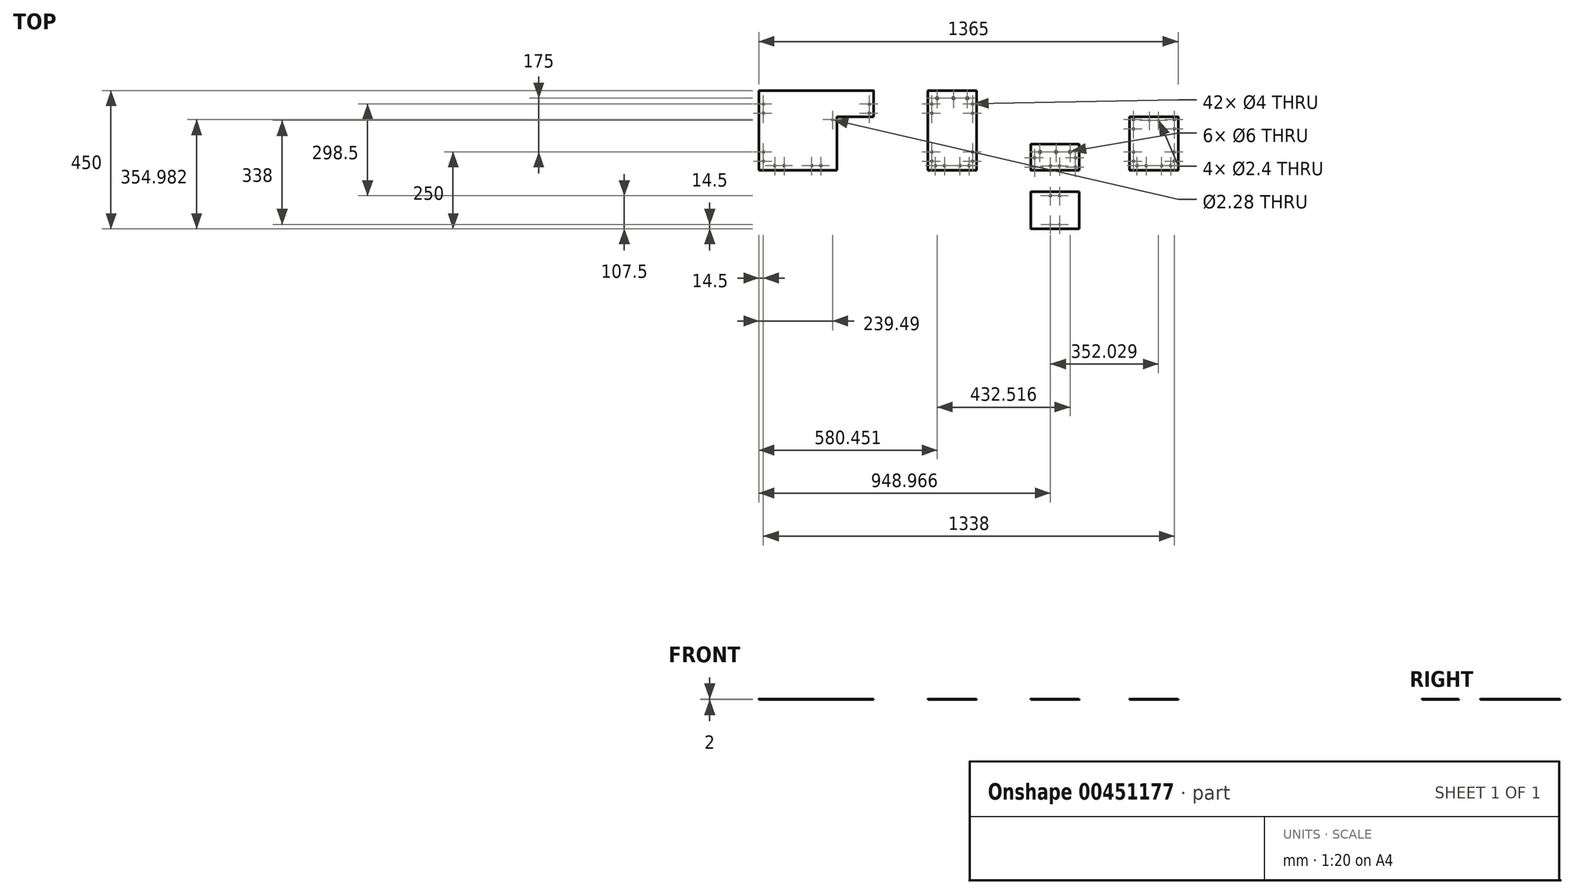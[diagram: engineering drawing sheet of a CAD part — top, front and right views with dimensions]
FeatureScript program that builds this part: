
annotation { "Feature Type Name" : "Feature", "Feature Type Description" : "" }
export const myFeature = defineFeature(function(context is Context, id is Id, definition is map)
    precondition{}
    {
        {
            var Q0;
            Q0=qCreatedBy(makeId("Top.planeOp"),FACE);
            var sketch = newSketch(context, id + "F0", { "sketchPlane" : qUnion([Q0])});
            skLineSegment(sketch, "E0.bottom", {"start": v(374, 0) * mm, "end": v(0, 0) * mm});
            skLineSegment(sketch, "E0.top", {"start": v(374, 260) * mm, "end": v(0, 260) * mm});
            skLineSegment(sketch, "E0.left", {"start": v(374, 0) * mm, "end": v(374, 260) * mm});
            skLineSegment(sketch, "E0.right", {"start": v(0, 0) * mm, "end": v(0, 260) * mm});
            skPoint(sketch, "E0.middle", {"position": v(187, 130) * mm});
            skLineSegment(sketch, "E1.bottom", {"start": v(708.45, 0) * mm, "end": v(550.45, 0) * mm});
            skLineSegment(sketch, "E1.top", {"start": v(708.45, 260) * mm, "end": v(550.45, 260) * mm});
            skLineSegment(sketch, "E1.left", {"start": v(708.45, 0) * mm, "end": v(708.45, 260) * mm});
            skLineSegment(sketch, "E1.right", {"start": v(550.45, 0) * mm, "end": v(550.45, 260) * mm});
            skPoint(sketch, "E1.middle", {"position": v(629.45, 130) * mm});
            skLineSegment(sketch, "E2.bottom", {"start": v(1042.97, 0) * mm, "end": v(884.97, 0) * mm});
            skLineSegment(sketch, "E2.top", {"start": v(1042.97, 85) * mm, "end": v(884.97, 85) * mm});
            skLineSegment(sketch, "E2.left", {"start": v(1042.97, 0) * mm, "end": v(1042.97, 85) * mm});
            skLineSegment(sketch, "E2.right", {"start": v(884.97, 0) * mm, "end": v(884.97, 85) * mm});
            skPoint(sketch, "E2.middle", {"position": v(963.97, 42.5) * mm});
            skLineSegment(sketch, "E3.bottom", {"start": v(1365, 175) * mm, "end": v(1207, 175) * mm});
            skLineSegment(sketch, "E3.top", {"start": v(1365, 0) * mm, "end": v(1207, 0) * mm});
            skLineSegment(sketch, "E3.left", {"start": v(1207, 0) * mm, "end": v(1207, 175) * mm});
            skLineSegment(sketch, "E3.right", {"start": v(1365, 0) * mm, "end": v(1365, 175) * mm});
            skPoint(sketch, "E3.middle", {"position": v(1286, 87.5) * mm});
            skCircle(sketch, "E4", {"center": v(62, 206) * mm, "radius": 1.5 * mm, "construction": true});
            skCircle(sketch, "E5", {"center": v(102, 206) * mm, "radius": 1.5 * mm, "construction": true});
            skLineSegment(sketch, "E6", {"start": v(187, 130) * mm, "end": v(187, 165.07) * mm, "construction": true});
            skLineSegment(sketch, "E7.bottom", {"start": v(917.97, 57) * mm, "end": v(911.97, 57) * mm, "construction": true});
            skLineSegment(sketch, "E7.top", {"start": v(917.97, 63) * mm, "end": v(911.97, 63) * mm, "construction": true});
            skLineSegment(sketch, "E7.left", {"start": v(917.97, 57) * mm, "end": v(917.97, 63) * mm, "construction": true});
            skLineSegment(sketch, "E7.right", {"start": v(911.97, 57) * mm, "end": v(911.97, 63) * mm, "construction": true});
            skPoint(sketch, "E7.middle", {"position": v(914.97, 60) * mm});
            skArc(sketch, "E8", {"start": v(917.97, 63) * mm, "mid": v(914.97, 66) * mm, "end": v(911.97, 63) * mm, "construction": true});
            skArc(sketch, "E9", {"start": v(911.97, 57) * mm, "mid": v(914.97, 54) * mm, "end": v(917.97, 57) * mm, "construction": true});
            skLineSegment(sketch, "E10.bottom", {"start": v(970.97, 57) * mm, "end": v(964.97, 57) * mm, "construction": true});
            skLineSegment(sketch, "E10.top", {"start": v(970.97, 63) * mm, "end": v(964.97, 63) * mm, "construction": true});
            skLineSegment(sketch, "E10.left", {"start": v(970.97, 57) * mm, "end": v(970.97, 63) * mm, "construction": true});
            skLineSegment(sketch, "E10.right", {"start": v(964.97, 57) * mm, "end": v(964.97, 63) * mm, "construction": true});
            skPoint(sketch, "E10.middle", {"position": v(967.97, 60) * mm});
            skArc(sketch, "E11", {"start": v(970.97, 63) * mm, "mid": v(967.97, 66) * mm, "end": v(964.97, 63) * mm, "construction": true});
            skArc(sketch, "E12", {"start": v(964.97, 57) * mm, "mid": v(967.97, 54) * mm, "end": v(970.97, 57) * mm, "construction": true});
            skLineSegment(sketch, "E13.bottom", {"start": v(1015.97, 57) * mm, "end": v(1009.97, 57) * mm, "construction": true});
            skLineSegment(sketch, "E13.top", {"start": v(1015.97, 63) * mm, "end": v(1009.97, 63) * mm, "construction": true});
            skLineSegment(sketch, "E13.left", {"start": v(1015.97, 57) * mm, "end": v(1015.97, 63) * mm, "construction": true});
            skLineSegment(sketch, "E13.right", {"start": v(1009.97, 57) * mm, "end": v(1009.97, 63) * mm, "construction": true});
            skPoint(sketch, "E13.middle", {"position": v(1012.97, 60) * mm});
            skArc(sketch, "E14", {"start": v(1015.97, 63) * mm, "mid": v(1012.97, 66) * mm, "end": v(1009.97, 63) * mm, "construction": true});
            skArc(sketch, "E15", {"start": v(1009.97, 57) * mm, "mid": v(1012.97, 54) * mm, "end": v(1015.97, 57) * mm, "construction": true});
            skLineSegment(sketch, "E16.bottom", {"start": v(64, 202) * mm, "end": v(60, 202) * mm, "construction": true});
            skLineSegment(sketch, "E16.top", {"start": v(64, 210) * mm, "end": v(60, 210) * mm, "construction": true});
            skLineSegment(sketch, "E16.left", {"start": v(64, 202) * mm, "end": v(64, 210) * mm, "construction": true});
            skLineSegment(sketch, "E16.right", {"start": v(60, 202) * mm, "end": v(60, 210) * mm, "construction": true});
            skArc(sketch, "E17", {"start": v(64, 210) * mm, "mid": v(62, 212) * mm, "end": v(60, 210) * mm, "construction": true});
            skArc(sketch, "E18", {"start": v(60, 202) * mm, "mid": v(62, 200) * mm, "end": v(64, 202) * mm, "construction": true});
            skLineSegment(sketch, "E19.bottom", {"start": v(104, 202) * mm, "end": v(100, 202) * mm, "construction": true});
            skLineSegment(sketch, "E19.top", {"start": v(104, 210) * mm, "end": v(100, 210) * mm, "construction": true});
            skLineSegment(sketch, "E19.left", {"start": v(104, 202) * mm, "end": v(104, 210) * mm, "construction": true});
            skLineSegment(sketch, "E19.right", {"start": v(100, 202) * mm, "end": v(100, 210) * mm, "construction": true});
            skArc(sketch, "E20", {"start": v(104, 210) * mm, "mid": v(102, 212) * mm, "end": v(100, 210) * mm, "construction": true});
            skArc(sketch, "E21", {"start": v(100, 202) * mm, "mid": v(102, 200) * mm, "end": v(104, 202) * mm, "construction": true});
            skLineSegment(sketch, "E22.MirrorCS", {"start": v(270, 210) * mm, "end": v(274, 210) * mm, "construction": true});
            skLineSegment(sketch, "E23.MirrorCS", {"start": v(270, 202) * mm, "end": v(274, 202) * mm, "construction": true});
            skArc(sketch, "E24.MirrorCS", {"start": v(274, 202) * mm, "mid": v(272, 200) * mm, "end": v(270, 202) * mm, "construction": true});
            skLineSegment(sketch, "E25.MirrorCS", {"start": v(274, 202) * mm, "end": v(274, 210) * mm, "construction": true});
            skLineSegment(sketch, "E26.MirrorCS", {"start": v(270, 202) * mm, "end": v(270, 210) * mm, "construction": true});
            skArc(sketch, "E27.MirrorCS", {"start": v(270, 210) * mm, "mid": v(272, 212) * mm, "end": v(274, 210) * mm, "construction": true});
            skPoint(sketch, "E28.MirrorP", {"position": v(272, 206) * mm});
            skArc(sketch, "E29.MirrorCS", {"start": v(314, 202) * mm, "mid": v(312, 200) * mm, "end": v(310, 202) * mm, "construction": true});
            skLineSegment(sketch, "E30.MirrorCS", {"start": v(310, 202) * mm, "end": v(314, 202) * mm, "construction": true});
            skLineSegment(sketch, "E31.MirrorCS", {"start": v(310, 210) * mm, "end": v(314, 210) * mm, "construction": true});
            skLineSegment(sketch, "E32.MirrorCS", {"start": v(314, 202) * mm, "end": v(314, 210) * mm, "construction": true});
            skLineSegment(sketch, "E33.MirrorCS", {"start": v(310, 202) * mm, "end": v(310, 210) * mm, "construction": true});
            skArc(sketch, "E34.MirrorCS", {"start": v(310, 210) * mm, "mid": v(312, 212) * mm, "end": v(314, 210) * mm, "construction": true});
            skPoint(sketch, "E35.MirrorP", {"position": v(312, 206) * mm});
            skCircle(sketch, "E36", {"center": v(580.45, 235) * mm, "radius": 3 * mm});
            skCircle(sketch, "E37", {"center": v(633.45, 235) * mm, "radius": 3 * mm});
            skCircle(sketch, "E38", {"center": v(678.45, 235) * mm, "radius": 3 * mm});
            skLineSegment(sketch, "E39.bottom", {"start": v(1042.97, -70) * mm, "end": v(884.97, -70) * mm});
            skLineSegment(sketch, "E39.top", {"start": v(1042.97, -190) * mm, "end": v(884.97, -190) * mm});
            skLineSegment(sketch, "E39.left", {"start": v(1042.97, -70) * mm, "end": v(1042.97, -190) * mm});
            skLineSegment(sketch, "E39.right", {"start": v(884.97, -70) * mm, "end": v(884.97, -190) * mm});
            skPoint(sketch, "E39.middle", {"position": v(963.97, -130) * mm});
            skCircle(sketch, "E40", {"center": v(914.97, 60) * mm, "radius": 3 * mm});
            skCircle(sketch, "E41", {"center": v(967.97, 60) * mm, "radius": 3 * mm});
            skCircle(sketch, "E42", {"center": v(1012.97, 60) * mm, "radius": 3 * mm});
            skCircle(sketch, "E43", {"center": v(574.45, 15.5) * mm, "radius": 2 * mm});
            skCircle(sketch, "E44", {"center": v(604.45, 15.5) * mm, "radius": 2 * mm});
            skLineSegment(sketch, "E45", {"start": v(629.45, 142.28) * mm, "end": v(629.45, 157.74) * mm, "construction": true});
            skCircle(sketch, "E46.MirrorC", {"center": v(684.45, 15.5) * mm, "radius": 2 * mm});
            skCircle(sketch, "E47.MirrorC", {"center": v(654.45, 15.5) * mm, "radius": 2 * mm});
            skCircle(sketch, "E48", {"center": v(1231, 15.5) * mm, "radius": 2 * mm});
            skCircle(sketch, "E49", {"center": v(1261, 15.5) * mm, "radius": 2 * mm});
            skLineSegment(sketch, "E50", {"start": v(1286, 97.83) * mm, "end": v(1286, 112.31) * mm, "construction": true});
            skCircle(sketch, "E51.MirrorC", {"center": v(1311, 15.5) * mm, "radius": 2 * mm});
            skCircle(sketch, "E52.MirrorC", {"center": v(1341, 15.5) * mm, "radius": 2 * mm});
            skCircle(sketch, "E53", {"center": v(695.95, 216) * mm, "radius": 2 * mm});
            skCircle(sketch, "E54", {"center": v(695.95, 186) * mm, "radius": 2 * mm});
            skLineSegment(sketch, "E55", {"start": v(689.83, 221) * mm, "end": v(700.87, 221) * mm, "construction": true});
            skCircle(sketch, "E56.MirrorC", {"center": v(562.95, 216) * mm, "radius": 2 * mm});
            skCircle(sketch, "E57.MirrorC", {"center": v(562.95, 186) * mm, "radius": 2 * mm});
            skLineSegment(sketch, "E58", {"start": v(648.13, 130) * mm, "end": v(662.37, 130) * mm, "construction": true});
            skCircle(sketch, "E59.MirrorC", {"center": v(695.95, 60) * mm, "radius": 2 * mm});
            skCircle(sketch, "E60.MirrorC", {"center": v(695.95, 30) * mm, "radius": 2 * mm});
            skCircle(sketch, "E61", {"center": v(1030.47, 41) * mm, "radius": 2 * mm});
            skCircle(sketch, "E62", {"center": v(1030.47, 11) * mm, "radius": 2 * mm});
            skLineSegment(sketch, "E63", {"start": v(963.97, 51.85) * mm, "end": v(963.97, 57.94) * mm, "construction": true});
            skCircle(sketch, "E64.MirrorC", {"center": v(897.47, 11) * mm, "radius": 2 * mm});
            skCircle(sketch, "E65.MirrorC", {"center": v(897.47, 41) * mm, "radius": 2 * mm});
            skCircle(sketch, "E66", {"center": v(1352.5, 60) * mm, "radius": 2 * mm});
            skCircle(sketch, "E67", {"center": v(1352.5, 30) * mm, "radius": 2 * mm});
            skCircle(sketch, "E68.MirrorC", {"center": v(1219.5, 30) * mm, "radius": 2 * mm});
            skCircle(sketch, "E69.MirrorC", {"center": v(1219.5, 60) * mm, "radius": 2 * mm});
            skCircle(sketch, "E70.MirrorC", {"center": v(562.95, 60) * mm, "radius": 2 * mm});
            skCircle(sketch, "E71.MirrorC", {"center": v(562.95, 30) * mm, "radius": 2 * mm});
            skCircle(sketch, "E72", {"center": v(1352.5, 165) * mm, "radius": 2 * mm});
            skCircle(sketch, "E73", {"center": v(1352.5, 135) * mm, "radius": 2 * mm});
            skCircle(sketch, "E74.MirrorC", {"center": v(1219.5, 135) * mm, "radius": 2 * mm});
            skCircle(sketch, "E75.MirrorC", {"center": v(1219.5, 165) * mm, "radius": 2 * mm});
            skCircle(sketch, "E76", {"center": v(14.5, 60) * mm, "radius": 2 * mm});
            skCircle(sketch, "E77", {"center": v(14.5, 30) * mm, "radius": 2 * mm});
            skCircle(sketch, "E78", {"center": v(14.5, 216) * mm, "radius": 2 * mm});
            skCircle(sketch, "E79", {"center": v(14.5, 186) * mm, "radius": 2 * mm});
            skCircle(sketch, "E80.MirrorC", {"center": v(359.5, 186) * mm, "radius": 2 * mm});
            skCircle(sketch, "E81.MirrorC", {"center": v(359.5, 216) * mm, "radius": 2 * mm});
            skCircle(sketch, "E82", {"center": v(978.97, 14.5) * mm, "radius": 2 * mm});
            skCircle(sketch, "E83", {"center": v(948.97, 14.5) * mm, "radius": 2 * mm});
            skCircle(sketch, "E84", {"center": v(948.97, -82.5) * mm, "radius": 2 * mm});
            skCircle(sketch, "E85", {"center": v(978.97, -82.5) * mm, "radius": 2 * mm});
            skCircle(sketch, "E86", {"center": v(948.97, -175.5) * mm, "radius": 1.2 * mm});
            skCircle(sketch, "E87", {"center": v(978.97, -175.5) * mm, "radius": 1.2 * mm});
            skCircle(sketch, "E88", {"center": v(1301, 162.5) * mm, "radius": 1.2 * mm});
            skCircle(sketch, "E89", {"center": v(1271, 162.5) * mm, "radius": 1.2 * mm});
            skCircle(sketch, "E90", {"center": v(239.5, 164.98) * mm, "radius": 1.14 * mm});
            skSolve(sketch);
        }
        {
            var Q0;
            Q0 = qSketchRegion(id + "F0", true);
            extrude(context, id + "F1", {"entities" : qUnion([Q0]), "depth" : 2 * mm, "offsetDistance" : 25 * mm});
        }
        {
            var Q0;
            Q0=makeQuery(id+"F1.opExtrude","CAP_FACE",FACE,{"disambiguationData":[OSD([sQuery(id+"F0.wireOp",EDGE,"E0.bottom"),sQuery(id+"F0.wireOp",EDGE,"E0.top"),sQuery(id+"F0.wireOp",EDGE,"E0.left"),sQuery(id+"F0.wireOp",EDGE,"E0.right"),sQuery(id+"F0.wireOp",EDGE,"E4"),sQuery(id+"F0.wireOp",EDGE,"E5"),sQuery(id+"F0.wireOp",EDGE,"4ba7c3d7-5d5b-46dc-9287-b6db8c2c33c00.MirrorC"),sQuery(id+"F0.wireOp",EDGE,"4ba7c3d7-5d5b-46dc-9287-b6db8c2c33c01.MirrorC")])],"isStart":false});
            var sketch = newSketch(context, id + "F2", { "sketchPlane" : qUnion([Q0])});
            skLineSegment(sketch, "E91.bottom", {"start": v(374, 0) * mm, "end": v(254, 0) * mm});
            skLineSegment(sketch, "E91.top", {"start": v(374, 175) * mm, "end": v(254, 175) * mm});
            skLineSegment(sketch, "E91.left", {"start": v(374, 0) * mm, "end": v(374, 175) * mm});
            skLineSegment(sketch, "E91.right", {"start": v(254, 0) * mm, "end": v(254, 175) * mm});
            skLineSegment(sketch, "E92", {"start": v(127, 64.28) * mm, "end": v(127, 23.94) * mm, "construction": true});
            skCircle(sketch, "E93", {"center": v(52, 15.5) * mm, "radius": 2 * mm});
            skCircle(sketch, "E94", {"center": v(82, 15.5) * mm, "radius": 2 * mm});
            skCircle(sketch, "E95.MirrorC", {"center": v(172, 15.5) * mm, "radius": 2 * mm});
            skCircle(sketch, "E96.MirrorC", {"center": v(202, 15.5) * mm, "radius": 2 * mm});
            skSolve(sketch);
        }
        {
            var Q0;
            Q0 = qSketchRegion(id + "F2", true);
            extrude(context, id + "F3", {"entities" : qUnion([Q0]), "operationType" : NewBodyOperationType.REMOVE, "oppositeDirection" : true, "depth" : 25 * mm, "offsetDistance" : 25 * mm});
        }
        {
            var Q0;
            Q0=makeQuery(id+"F1.opExtrude","SWEPT_EDGE",EDGE,{"disambiguationData":[OSD([sQuery(id+"F0.wireOp",EDGE,"E2.top"),sQuery(id+"F0.wireOp",EDGE,"E2.left")])]});
            var Q1;
            Q1=makeQuery(id+"F1.opExtrude","SWEPT_EDGE",EDGE,{"disambiguationData":[OSD([sQuery(id+"F0.wireOp",EDGE,"E2.bottom"),sQuery(id+"F0.wireOp",EDGE,"E2.left")])]});
            var Q2;
            Q2=makeQuery(id+"F1.opExtrude","SWEPT_EDGE",EDGE,{"disambiguationData":[OSD([sQuery(id+"F0.wireOp",EDGE,"E2.bottom"),sQuery(id+"F0.wireOp",EDGE,"E2.right")])]});
            var Q3;
            Q3=makeQuery(id+"F1.opExtrude","SWEPT_EDGE",EDGE,{"disambiguationData":[OSD([sQuery(id+"F0.wireOp",EDGE,"E2.top"),sQuery(id+"F0.wireOp",EDGE,"E2.right")])]});
            var Q4;
            Q4=makeQuery(id+"F1.opExtrude","SWEPT_EDGE",EDGE,{"disambiguationData":[OSD([sQuery(id+"F0.wireOp",EDGE,"E0.top"),sQuery(id+"F0.wireOp",EDGE,"E0.right")])]});
            var Q5;
            Q5=makeQuery(id+"F1.opExtrude","SWEPT_EDGE",EDGE,{"disambiguationData":[OSD([sQuery(id+"F0.wireOp",EDGE,"E0.bottom"),sQuery(id+"F0.wireOp",EDGE,"E0.right")])]});
            var Q6;
            Q6=makeQuery(id+"F3.boolean.opBoolean","COPY",EDGE,{"derivedFrom":makeQuery(id+"F3.opExtrude","SWEPT_EDGE",EDGE,{"disambiguationData":[OSD([sQuery(id+"F0.wireOp",EDGE,"E0.bottom"),sQuery(id+"F2.wireOp",EDGE,"E91.bottom"),sQuery(id+"F2.wireOp",EDGE,"E91.right")])]})});
            var Q7;
            Q7=makeQuery(id+"F3.boolean.opBoolean","COPY",EDGE,{"derivedFrom":makeQuery(id+"F3.opExtrude","SWEPT_EDGE",EDGE,{"disambiguationData":[OSD([sQuery(id+"F2.wireOp",EDGE,"E91.top"),sQuery(id+"F2.wireOp",EDGE,"E91.right")])]})});
            var Q8;
            Q8=makeQuery(id+"F3.boolean.opBoolean","COPY",EDGE,{"derivedFrom":makeQuery(id+"F3.opExtrude","SWEPT_EDGE",EDGE,{"disambiguationData":[OSD([sQuery(id+"F0.wireOp",EDGE,"E0.left"),sQuery(id+"F2.wireOp",EDGE,"E91.top"),sQuery(id+"F2.wireOp",EDGE,"E91.left")])]})});
            var Q9;
            Q9=makeQuery(id+"F1.opExtrude","SWEPT_EDGE",EDGE,{"disambiguationData":[OSD([sQuery(id+"F0.wireOp",EDGE,"E0.top"),sQuery(id+"F0.wireOp",EDGE,"E0.left")])]});
            var Q10;
            Q10=makeQuery(id+"F1.opExtrude","SWEPT_EDGE",EDGE,{"disambiguationData":[OSD([sQuery(id+"F0.wireOp",EDGE,"E1.top"),sQuery(id+"F0.wireOp",EDGE,"E1.right")])]});
            var Q11;
            Q11=makeQuery(id+"F1.opExtrude","SWEPT_EDGE",EDGE,{"disambiguationData":[OSD([sQuery(id+"F0.wireOp",EDGE,"E1.top"),sQuery(id+"F0.wireOp",EDGE,"E1.left")])]});
            var Q12;
            Q12=makeQuery(id+"F1.opExtrude","SWEPT_EDGE",EDGE,{"disambiguationData":[OSD([sQuery(id+"F0.wireOp",EDGE,"E1.bottom"),sQuery(id+"F0.wireOp",EDGE,"E1.left")])]});
            var Q13;
            Q13=makeQuery(id+"F1.opExtrude","SWEPT_EDGE",EDGE,{"disambiguationData":[OSD([sQuery(id+"F0.wireOp",EDGE,"E1.bottom"),sQuery(id+"F0.wireOp",EDGE,"E1.right")])]});
            var Q14;
            Q14=makeQuery(id+"F1.opExtrude","SWEPT_EDGE",EDGE,{"disambiguationData":[OSD([sQuery(id+"F0.wireOp",EDGE,"E39.bottom"),sQuery(id+"F0.wireOp",EDGE,"E39.right")])]});
            var Q15;
            Q15=makeQuery(id+"F1.opExtrude","SWEPT_EDGE",EDGE,{"disambiguationData":[OSD([sQuery(id+"F0.wireOp",EDGE,"E39.top"),sQuery(id+"F0.wireOp",EDGE,"E39.right")])]});
            var Q16;
            Q16=makeQuery(id+"F1.opExtrude","SWEPT_EDGE",EDGE,{"disambiguationData":[OSD([sQuery(id+"F0.wireOp",EDGE,"E39.bottom"),sQuery(id+"F0.wireOp",EDGE,"E39.left")])]});
            var Q17;
            Q17=makeQuery(id+"F1.opExtrude","SWEPT_EDGE",EDGE,{"disambiguationData":[OSD([sQuery(id+"F0.wireOp",EDGE,"E39.top"),sQuery(id+"F0.wireOp",EDGE,"E39.left")])]});
            var Q18;
            Q18=makeQuery(id+"F1.opExtrude","SWEPT_EDGE",EDGE,{"disambiguationData":[OSD([sQuery(id+"F0.wireOp",EDGE,"E3.bottom"),sQuery(id+"F0.wireOp",EDGE,"E3.left")])]});
            var Q19;
            Q19=makeQuery(id+"F1.opExtrude","SWEPT_EDGE",EDGE,{"disambiguationData":[OSD([sQuery(id+"F0.wireOp",EDGE,"E3.top"),sQuery(id+"F0.wireOp",EDGE,"E3.left")])]});
            var Q20;
            Q20=makeQuery(id+"F1.opExtrude","SWEPT_EDGE",EDGE,{"disambiguationData":[OSD([sQuery(id+"F0.wireOp",EDGE,"E3.bottom"),sQuery(id+"F0.wireOp",EDGE,"E3.right")])]});
            var Q21;
            Q21=makeQuery(id+"F1.opExtrude","SWEPT_EDGE",EDGE,{"disambiguationData":[OSD([sQuery(id+"F0.wireOp",EDGE,"E3.top"),sQuery(id+"F0.wireOp",EDGE,"E3.right")])]});
            fillet(context, id + "F4", {"entities" : qUnion([Q0, Q1, Q2, Q3, Q4, Q5, Q6, Q7, Q8, Q9, Q10, Q11, Q12, Q13, Q14, Q15, Q16, Q17, Q18, Q19, Q20, Q21]), "tangentPropagation" : true, "radius" : 1 * mm, "defaultsChanged" : false, "vertexSettings" : [], "allowEdgeOverflow" : false});
        }
    });
